# Revit family: WTB_WashTrough
name_source: partatom
category: Plumbing Fixtures
units: mm (PartAtom-declared; Revit-internal decimal feet)

## family parameters
Always vertical = Yes
Cut with Voids When Loaded = No
Host = Wall
OmniClass Number = 23.45.00.00
OmniClass Title = Sanitary, Laundry, and Cleaning Equipment
Part Type = Normal
Room Calculation Point = No
Round Connector Dimension = Use Diameter
Shared = No

## types (6) — shared parameters
Assembly = Fabricated
Brand = Mercer
Default Elevation = 810 mm
Description = Wash Trough all Radius Corners
Finish = Satin
Includes = Brackets
Material = 1.2mm 304 Stainless Steel
Model = WT Series
Moutning = Wall mounting brackets supplied
Wash Through Material = Stainless Steel
Waste = Flat 40mm outlet

## per-type parameters (varying)
| type | Manufacturer | Upstand Length | Wash Length Input |
| WTB600L | Mercer | 597.6 mm  [stored 1.96063 ft] | 600 mm  [stored 1.9685 ft] |
| WTB900L | Mercer | 897.6 mm  [stored 2.94488 ft] | 900 mm  [stored 2.95276 ft] |
| WTB1200L | Mercer | 1197.6 mm | 1200 mm |
| WTB1500L | Mercer | 1497.6 mm | 1500 mm  [stored 4.92126 ft] |
| WTB1800L |  | 1797.6 mm | 1800 mm  [stored 5.90551 ft] |
| WTB2100L | Mercer | 2097.6 mm | 2100 mm |

note: [stored X ft] marks values corroborated as IEEE doubles in the binary element streams (Revit-internal decimal feet)

## geometry (parser evidence)
native form markers: Sweep x5
no freeform markers — native parametric forms only
